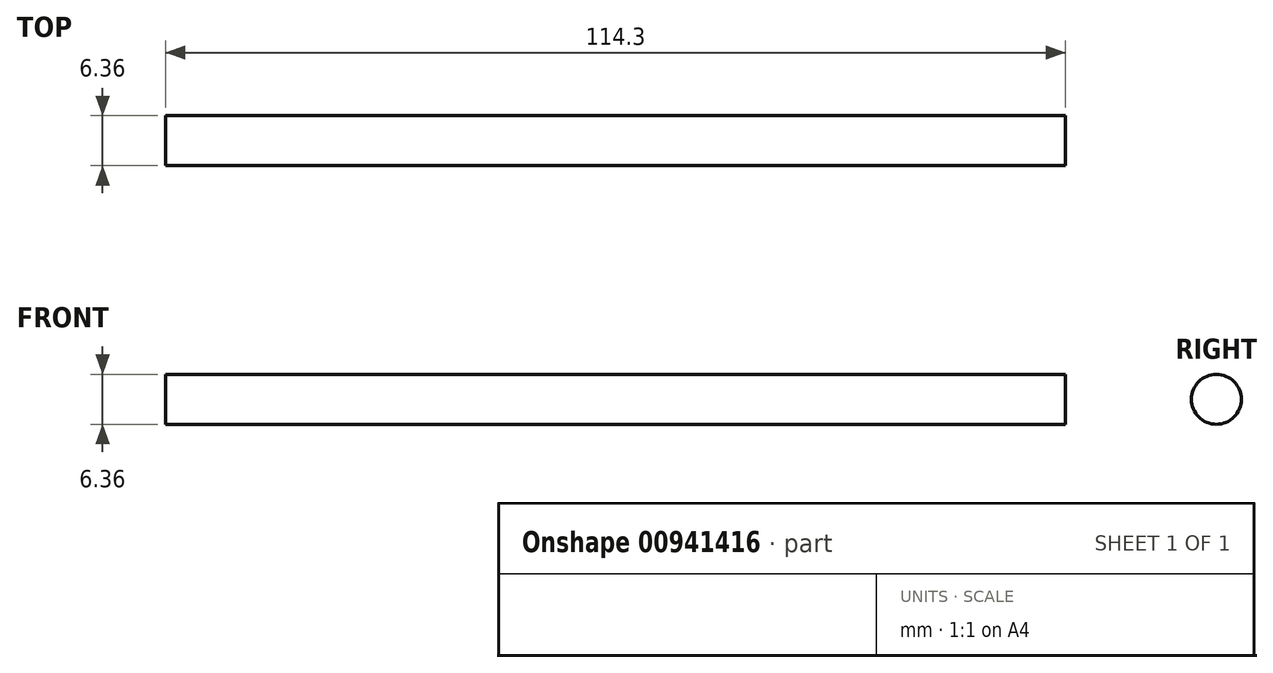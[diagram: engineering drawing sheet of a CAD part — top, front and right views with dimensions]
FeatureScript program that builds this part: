
annotation { "Feature Type Name" : "Feature", "Feature Type Description" : "" }
export const myFeature = defineFeature(function(context is Context, id is Id, definition is map)
    precondition{}
    {
        {
            var Q0;
            Q0=qCreatedBy(makeId("Right.planeOp"),FACE);
            var sketch = newSketch(context, id + "F0", { "sketchPlane" : qUnion([Q0])});
            skCircle(sketch, "E0", {"center": v(0, 0) * mm, "radius": 3.18 * mm});
            skSolve(sketch);
        }
        {
            var Q0;
            Q0=makeQuery(id+"F0.imprint","IMPRINT",FACE,{"disambiguationData":[TD([[makeQuery(id+"F0.imprint","IMPRINT",EDGE,{"derivedFrom":sQuery(id+"F0.wireOp",EDGE,"E0")}),1.0]])]});
            extrude(context, id + "F1", {"entities" : qUnion([Q0]), "depth" : 114.3 * mm, "offsetDistance" : 25.4 * mm});
        }
    });
